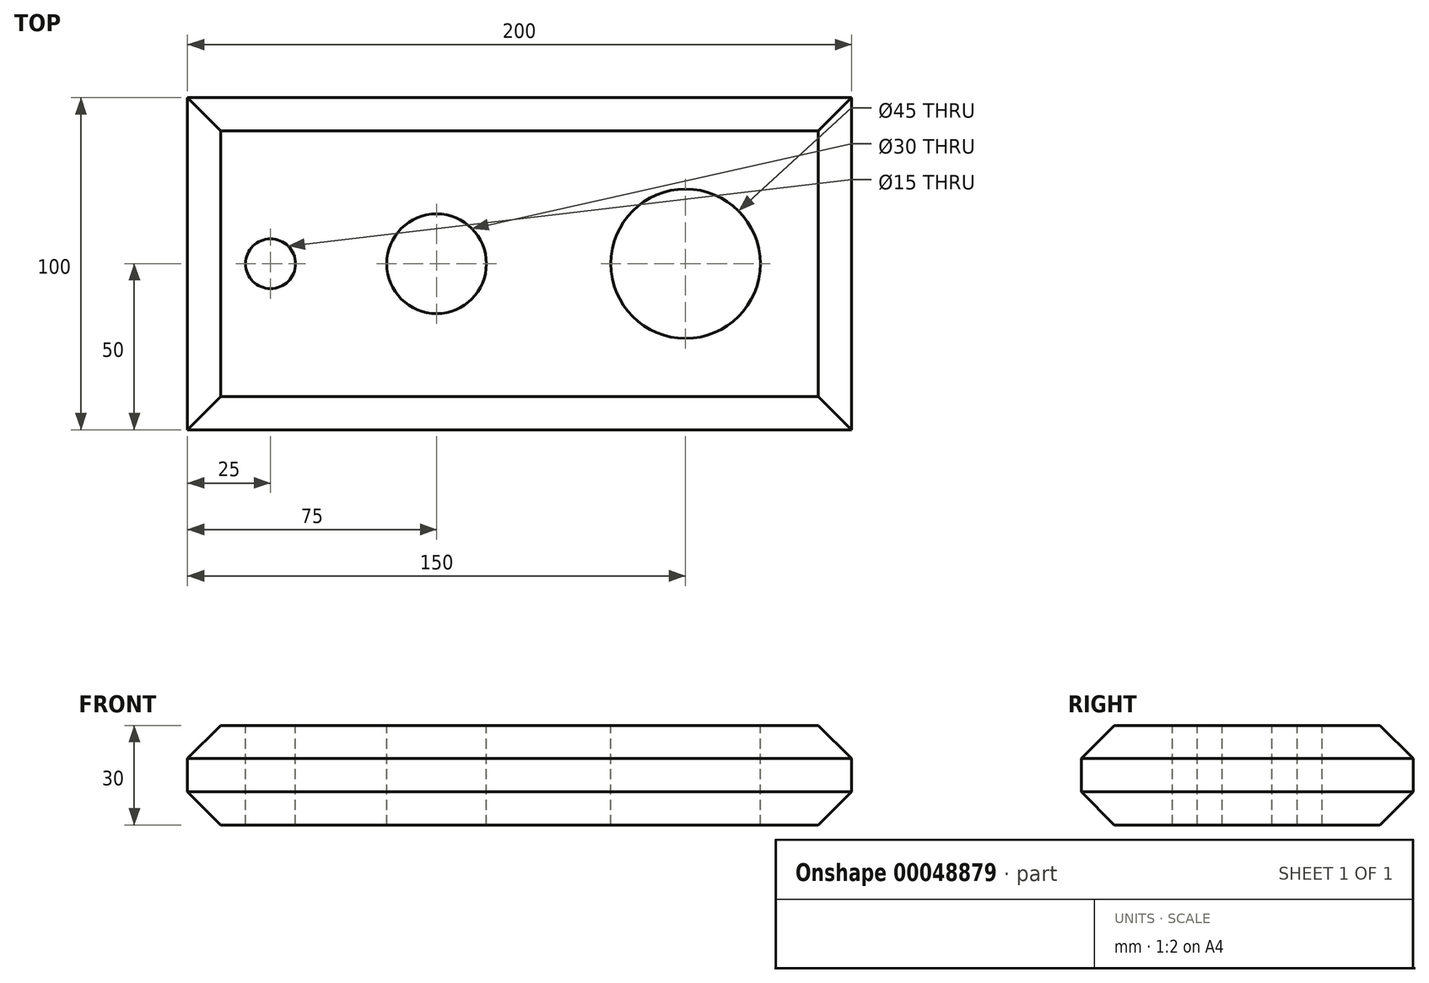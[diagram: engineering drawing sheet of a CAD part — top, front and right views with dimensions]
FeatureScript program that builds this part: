
annotation { "Feature Type Name" : "Feature", "Feature Type Description" : "" }
export const myFeature = defineFeature(function(context is Context, id is Id, definition is map)
    precondition{}
    {
        {
            var Q0;
            Q0=qCreatedBy(makeId("Top.planeOp"),FACE);
            var sketch = newSketch(context, id + "F0", { "sketchPlane" : qUnion([Q0])});
            skLineSegment(sketch, "E0.rect.bottom", {"start": v(100, 50) * mm, "end": v(-100, 50) * mm});
            skLineSegment(sketch, "E0.rect.top", {"start": v(100, -50) * mm, "end": v(-100, -50) * mm});
            skLineSegment(sketch, "E0.rect.left", {"start": v(100, 50) * mm, "end": v(100, -50) * mm});
            skLineSegment(sketch, "E0.rect.right", {"start": v(-100, 50) * mm, "end": v(-100, -50) * mm});
            skPoint(sketch, "E0.rect.middle", {"position": v(0, 0) * mm});
            skSolve(sketch);
        }
        {
            var Q0;
            Q0=makeQuery(id+"F0.imprint","IMPRINT",FACE,{"disambiguationData":[TD([[makeQuery(id+"F0.imprint","IMPRINT",EDGE,{"derivedFrom":sQuery(id+"F0.wireOp",EDGE,"E0.rect.bottom")}),1.0]])]});
            extrude(context, id + "F1", {"entities" : qUnion([Q0]), "depth" : 30 * mm});
        }
        {
            var Q0;
            Q0=makeQuery(id+"F1.opExtrude","CAP_FACE",FACE,{"disambiguationData":[OSD([sQuery(id+"F0.wireOp",EDGE,"E0.rect.bottom"),sQuery(id+"F0.wireOp",EDGE,"E0.rect.top"),sQuery(id+"F0.wireOp",EDGE,"E0.rect.left"),sQuery(id+"F0.wireOp",EDGE,"E0.rect.right")])],"isStart":false});
            var sketch = newSketch(context, id + "F2", { "sketchPlane" : qUnion([Q0])});
            skLineSegment(sketch, "E1", {"start": v(-100, 0) * mm, "end": v(-75, 0) * mm, "construction": true});
            skCircle(sketch, "E2", {"center": v(-75, 0) * mm, "radius": 7.5 * mm});
            skLineSegment(sketch, "E3", {"start": v(-75, 0) * mm, "end": v(-25, 0) * mm, "construction": true});
            skCircle(sketch, "E4", {"center": v(-25, 0) * mm, "radius": 15 * mm});
            skLineSegment(sketch, "E5", {"start": v(-25, 0) * mm, "end": v(50, 0) * mm, "construction": true});
            skCircle(sketch, "E6", {"center": v(50, 0) * mm, "radius": 22.5 * mm});
            skSolve(sketch);
        }
        {
            var Q0;
            Q0=makeQuery(id+"F1.opExtrude","CAP_EDGE",EDGE,{"disambiguationData":[OSD([sQuery(id+"F0.wireOp",EDGE,"E0.rect.top")])],"isStart":false});
            var Q1;
            Q1=makeQuery(id+"F1.opExtrude","CAP_EDGE",EDGE,{"disambiguationData":[OSD([sQuery(id+"F0.wireOp",EDGE,"E0.rect.left")])],"isStart":false});
            var Q2;
            Q2=makeQuery(id+"F1.opExtrude","CAP_EDGE",EDGE,{"disambiguationData":[OSD([sQuery(id+"F0.wireOp",EDGE,"E0.rect.bottom")])],"isStart":false});
            var Q3;
            Q3=makeQuery(id+"F1.opExtrude","CAP_EDGE",EDGE,{"disambiguationData":[OSD([sQuery(id+"F0.wireOp",EDGE,"E0.rect.right")])],"isStart":false});
            var Q4;
            Q4=makeQuery(id+"F1.opExtrude","CAP_EDGE",EDGE,{"disambiguationData":[OSD([sQuery(id+"F0.wireOp",EDGE,"E0.rect.top")])],"isStart":true});
            var Q5;
            Q5=makeQuery(id+"F1.opExtrude","CAP_EDGE",EDGE,{"disambiguationData":[OSD([sQuery(id+"F0.wireOp",EDGE,"E0.rect.left")])],"isStart":true});
            var Q6;
            Q6=makeQuery(id+"F1.opExtrude","CAP_EDGE",EDGE,{"disambiguationData":[OSD([sQuery(id+"F0.wireOp",EDGE,"E0.rect.right")])],"isStart":true});
            var Q7;
            Q7=makeQuery(id+"F1.opExtrude","CAP_EDGE",EDGE,{"disambiguationData":[OSD([sQuery(id+"F0.wireOp",EDGE,"E0.rect.bottom")])],"isStart":true});
            chamfer(context, id + "F3", {"entities" : qUnion([Q0, Q1, Q2, Q3, Q4, Q5, Q6, Q7]), "chamferType" : ChamferType.OFFSET_ANGLE, "width" : 10 * mm, "oppositeDirection" : false, "angle" : 45 * degree, "tangentPropagation" : true});
        }
        {
            var Q0;
            Q0=makeQuery(id+"F2.imprint","IMPRINT",FACE,{"disambiguationData":[TD([[makeQuery(id+"F2.imprint","IMPRINT",EDGE,{"derivedFrom":sQuery(id+"F2.wireOp",EDGE,"E2")}),1.0]])]});
            var Q1;
            Q1=makeQuery(id+"F2.imprint","IMPRINT",FACE,{"disambiguationData":[TD([[makeQuery(id+"F2.imprint","IMPRINT",EDGE,{"derivedFrom":sQuery(id+"F2.wireOp",EDGE,"E4")}),1.0]])]});
            var Q2;
            Q2=makeQuery(id+"F2.imprint","IMPRINT",FACE,{"disambiguationData":[TD([[makeQuery(id+"F2.imprint","IMPRINT",EDGE,{"derivedFrom":sQuery(id+"F2.wireOp",EDGE,"E6")}),1.0]])]});
            var Q3;
            Q3=sQuery(id+"F2.wireOp",EDGE,"E2");
            var Q4;
            Q4=sQuery(id+"F2.wireOp",EDGE,"E4");
            var Q5;
            Q5=sQuery(id+"F2.wireOp",EDGE,"E6");
            extrude(context, id + "F4", {"entities" : qUnion([Q0, Q1, Q2]), "operationType" : NewBodyOperationType.REMOVE, "surfaceEntities" : qUnion([Q3, Q4, Q5]), "endBound" : BoundingType.THROUGH_ALL, "oppositeDirection" : true, "depth" : 25 * mm});
        }
    });
